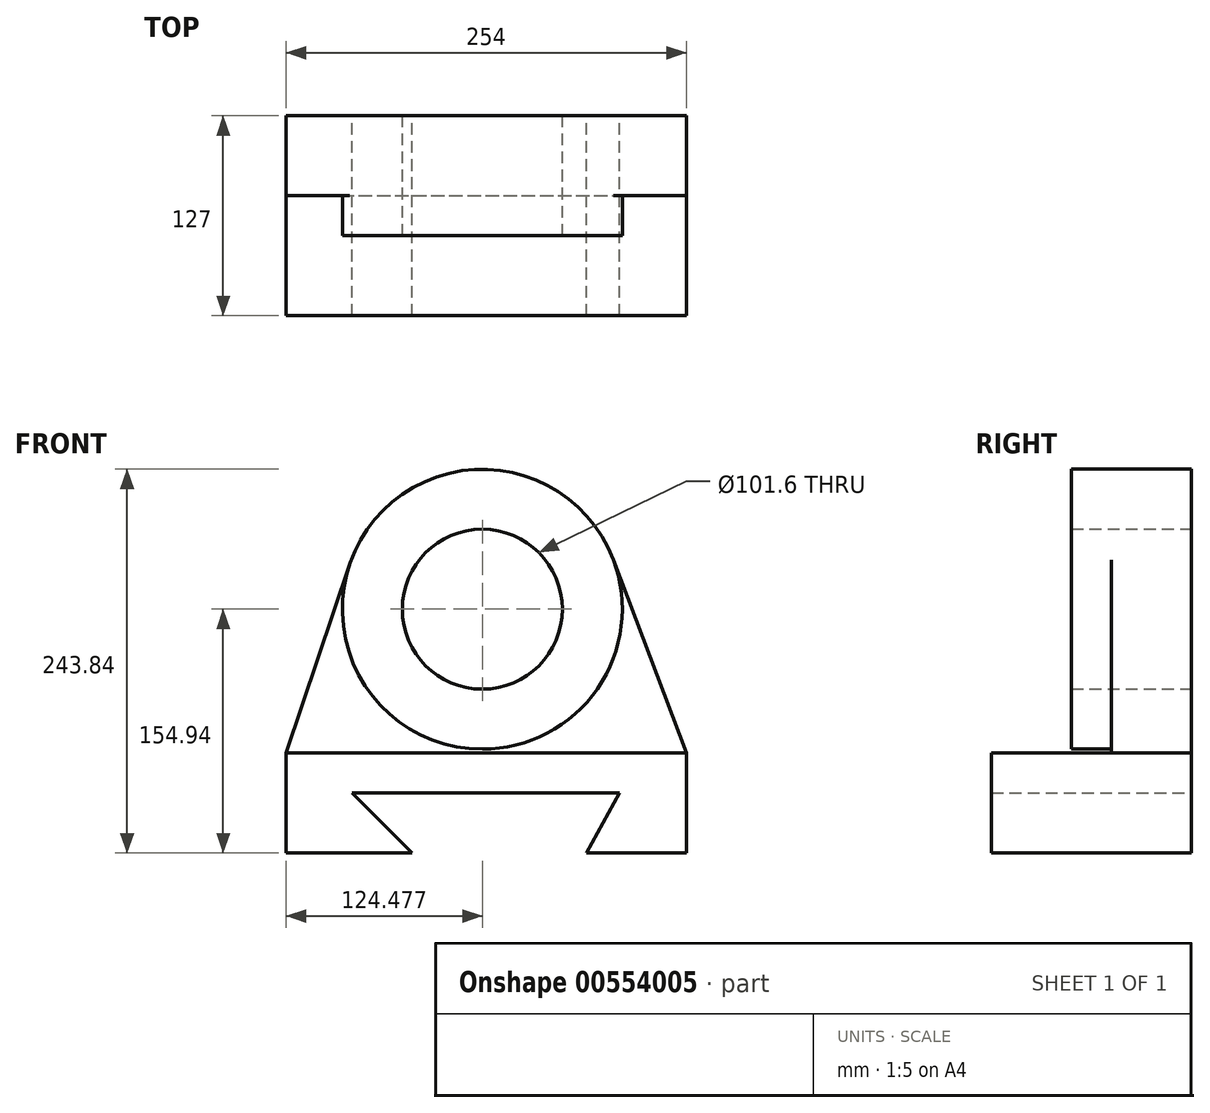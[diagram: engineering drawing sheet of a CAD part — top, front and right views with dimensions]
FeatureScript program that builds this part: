
annotation { "Feature Type Name" : "Feature", "Feature Type Description" : "" }
export const myFeature = defineFeature(function(context is Context, id is Id, definition is map)
    precondition{}
    {
        {
            var Q0;
            Q0=qCreatedBy(makeId("Front.planeOp"),FACE);
            var sketch = newSketch(context, id + "F0", { "sketchPlane" : qUnion([Q0])});
            skLineSegment(sketch, "E0", {"start": v(0, 0) * mm, "end": v(254, 0) * mm});
            skLineSegment(sketch, "E1", {"start": v(0, 0) * mm, "end": v(40.2, 119.74) * mm});
            skLineSegment(sketch, "E2", {"start": v(254, 0) * mm, "end": v(207.65, 122.83) * mm});
            skCircle(sketch, "E3", {"center": v(124.48, 91.44) * mm, "radius": 88.9 * mm});
            skPoint(sketch, "E4.orphan", {"position": v(68.8, 204.92) * mm});
            skPoint(sketch, "E5.orphan", {"position": v(176.67, 204.92) * mm});
            skCircle(sketch, "E6", {"center": v(124.48, 91.44) * mm, "radius": 50.8 * mm});
            skLineSegment(sketch, "E7", {"start": v(254, 0) * mm, "end": v(254, -63.5) * mm});
            skLineSegment(sketch, "E8", {"start": v(0, 0) * mm, "end": v(0, -63.5) * mm});
            skLineSegment(sketch, "E9", {"start": v(0, -63.5) * mm, "end": v(79.84, -63.5) * mm});
            skLineSegment(sketch, "E10", {"start": v(79.84, -63.5) * mm, "end": v(41.74, -25.4) * mm});
            skLineSegment(sketch, "E11", {"start": v(41.74, -25.4) * mm, "end": v(211.62, -25.4) * mm});
            skLineSegment(sketch, "E12", {"start": v(211.62, -25.4) * mm, "end": v(190.5, -63.5) * mm});
            skLineSegment(sketch, "E13", {"start": v(190.5, -63.5) * mm, "end": v(254, -63.5) * mm});
            skSolve(sketch);
        }
        {
            var Q0;
            {var subQ1=sQuery(id+"F0.wireOp",EDGE,"E7");Q0=makeQuery(id+"F0.imprint","IMPRINT",FACE,{"disambiguationData":[TD([[makeQuery(id+"F0.imprint","IMPRINT",EDGE,{"derivedFrom":subQ1}),-1.0]])]});}
            extrude(context, id + "F1", {"entities" : qUnion([Q0]), "depth" : 127 * mm, "offsetDistance" : 25.4 * mm});
        }
        {
            var Q0;
            {var subQ0=sQuery(id+"F0.wireOp",EDGE,"E1");Q0=makeQuery(id+"F0.imprint","IMPRINT",FACE,{"disambiguationData":[TD([[makeQuery(id+"F0.imprint","IMPRINT",EDGE,{"derivedFrom":subQ0}),-1.0]])]});}
            var Q1;
            {var subQ0=sQuery(id+"F0.wireOp",EDGE,"E2");Q1=makeQuery(id+"F0.imprint","IMPRINT",FACE,{"disambiguationData":[TD([[makeQuery(id+"F0.imprint","IMPRINT",EDGE,{"derivedFrom":subQ0}),1.0]])]});}
            extrude(context, id + "F2", {"entities" : qUnion([Q0, Q1]), "operationType" : NewBodyOperationType.ADD, "depth" : 50.8 * mm, "offsetDistance" : 25.4 * mm});
        }
        {
            var Q0;
            Q0=makeQuery(id+"F0.imprint","IMPRINT",FACE,{"disambiguationData":[TD([[makeQuery(id+"F0.imprint","IMPRINT",EDGE,{"derivedFrom":sQuery(id+"F0.wireOp",EDGE,"E6")}),-1.0]])]});
            extrude(context, id + "F3", {"entities" : qUnion([Q0]), "operationType" : NewBodyOperationType.ADD, "depth" : 25.4 * mm, "offsetDistance" : 25.4 * mm});
        }
        {
            var Q0;
            Q0=makeQuery(id+"F3.opExtrude","CAP_FACE",FACE,{"disambiguationData":[OSD([sQuery(id+"F0.wireOp",EDGE,"E3"),sQuery(id+"F0.wireOp",EDGE,"E6")])],"isStart":false});
            extrude(context, id + "F4", {"entities" : qUnion([Q0]), "operationType" : NewBodyOperationType.ADD, "depth" : 50.8 * mm, "offsetDistance" : 25.4 * mm});
        }
    });
